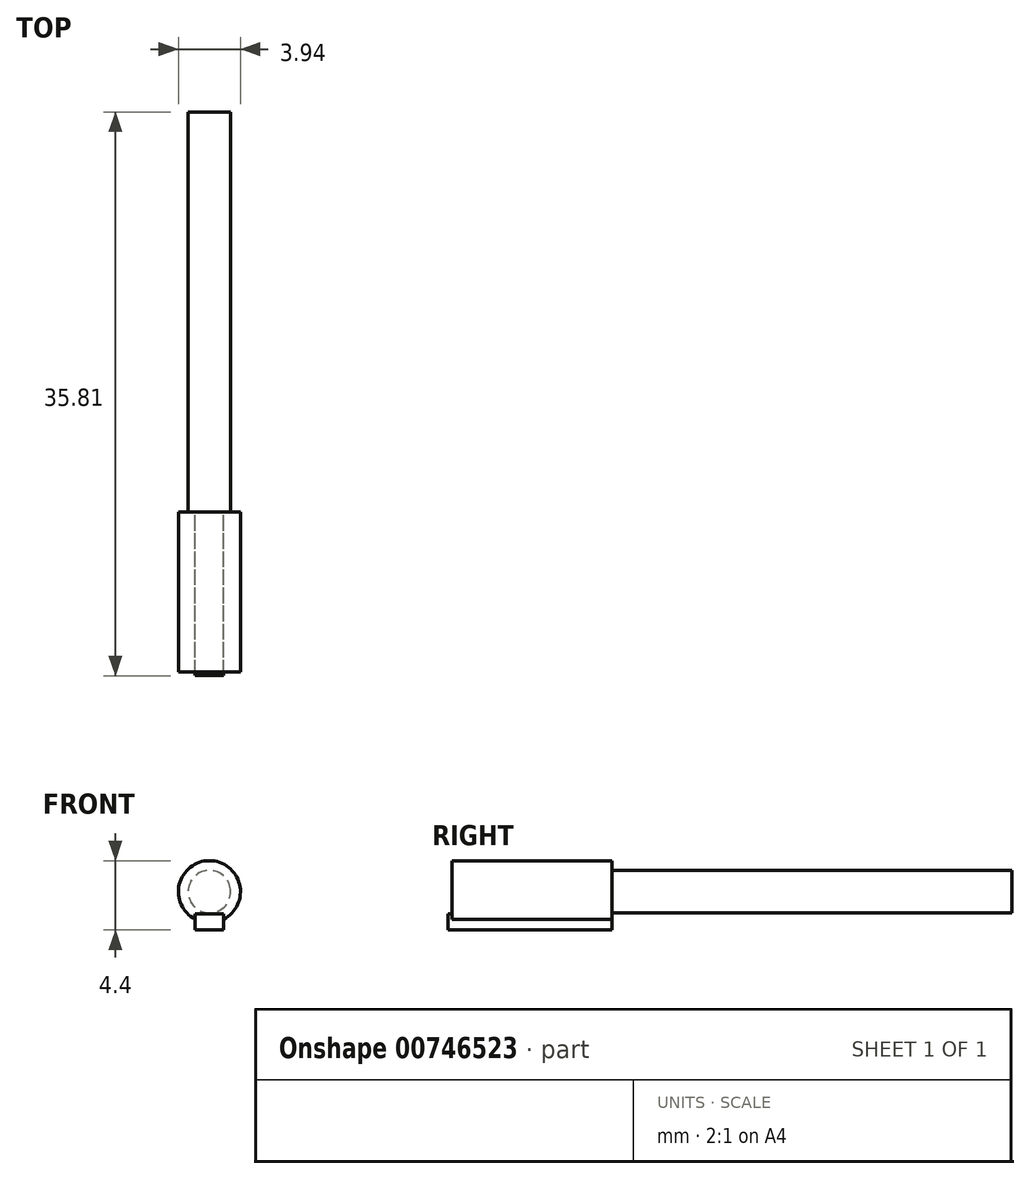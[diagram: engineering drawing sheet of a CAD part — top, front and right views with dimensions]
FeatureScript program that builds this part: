
annotation { "Feature Type Name" : "Feature", "Feature Type Description" : "" }
export const myFeature = defineFeature(function(context is Context, id is Id, definition is map)
    precondition{}
    {
        {
            var Q0;
            Q0=qCreatedBy(makeId("Top.planeOp"),FACE);
            var sketch = newSketch(context, id + "F0", { "sketchPlane" : qUnion([Q0])});
            skLineSegment(sketch, "E0.bottom", {"start": v(-49.1, 18.33) * mm, "end": v(-50.91, 18.33) * mm});
            skLineSegment(sketch, "E0.top", {"start": v(-49.1, 28.74) * mm, "end": v(-50.91, 28.74) * mm});
            skLineSegment(sketch, "E0.left", {"start": v(-49.1, 18.33) * mm, "end": v(-49.1, 28.74) * mm});
            skLineSegment(sketch, "E0.right", {"start": v(-50.91, 18.33) * mm, "end": v(-50.91, 28.74) * mm});
            skSolve(sketch);
        }
        {
            var Q0;
            Q0=makeQuery(id+"F0.imprint","IMPRINT",FACE,{"disambiguationData":[TD([[makeQuery(id+"F0.imprint","IMPRINT",EDGE,{"derivedFrom":sQuery(id+"F0.wireOp",EDGE,"E0.bottom")}),-1.0]])]});
            extrude(context, id + "F1", {"entities" : qUnion([Q0]), "depth" : 1.02 * mm, "offsetDistance" : 25.4 * mm});
        }
        {
            var Q0;
            Q0=makeQuery(id+"F1.opExtrude","SWEPT_FACE",FACE,{"disambiguationData":[OSD([sQuery(id+"F0.wireOp",EDGE,"E0.top")])]});
            var sketch = newSketch(context, id + "F2", { "sketchPlane" : qUnion([Q0])});
            skCircle(sketch, "E1", {"center": v(50, 2.44) * mm, "radius": 1.97 * mm});
            skPoint(sketch, "E1.centerSnap0", {"position": v(50, 1.02) * mm});
            skSolve(sketch);
        }
        {
            var Q0;
            {var subQ1=sQuery(id+"F0.wireOp",EDGE,"E0.top");var subQ6=makeQuery(id+"F1.opExtrude","CAP_EDGE",EDGE,{"disambiguationData":[OSD([subQ1])],"isStart":false});Q0=makeQuery(id+"F2.imprint","IMPRINT",FACE,{"disambiguationData":[TD([[makeQuery(id+"F2.imprint","IMPRINT",EDGE,{"derivedFrom":subQ6}),1.0]])]});}
            extrude(context, id + "F3", {"entities" : qUnion([Q0]), "operationType" : NewBodyOperationType.ADD, "oppositeDirection" : true, "depth" : 10.16 * mm, "offsetDistance" : 25.4 * mm});
        }
        {
            var Q0;
            {var subQ0=sQuery(id+"F0.wireOp",EDGE,"E0.top");Q0=makeQuery(id+"F3.boolean.opBoolean","MERGE",FACE,{"derivedFrom":[makeQuery(id+"F1.opExtrude","SWEPT_FACE",FACE,{"disambiguationData":[OSD([subQ0])]}),makeQuery(id+"F3.opExtrude","CAP_FACE",FACE,{"disambiguationData":[OSD([subQ0,sQuery(id+"F0.wireOp",EDGE,"E0.left"),sQuery(id+"F0.wireOp",EDGE,"E0.right"),sQuery(id+"F2.wireOp",EDGE,"E1")])],"isStart":true})]});}
            var sketch = newSketch(context, id + "F4", { "sketchPlane" : qUnion([Q0])});
            skCircle(sketch, "E2", {"center": v(50, 2.44) * mm, "radius": 1.35 * mm});
            skSolve(sketch);
        }
        {
            var Q0;
            Q0=makeQuery(id+"F4.imprint","IMPRINT",FACE,{"disambiguationData":[TD([[makeQuery(id+"F4.imprint","IMPRINT",EDGE,{"derivedFrom":sQuery(id+"F4.wireOp",EDGE,"E2")}),1.0]])]});
            extrude(context, id + "F5", {"entities" : qUnion([Q0]), "operationType" : NewBodyOperationType.ADD, "depth" : 25.4 * mm, "offsetDistance" : 25.4 * mm});
        }
    });
